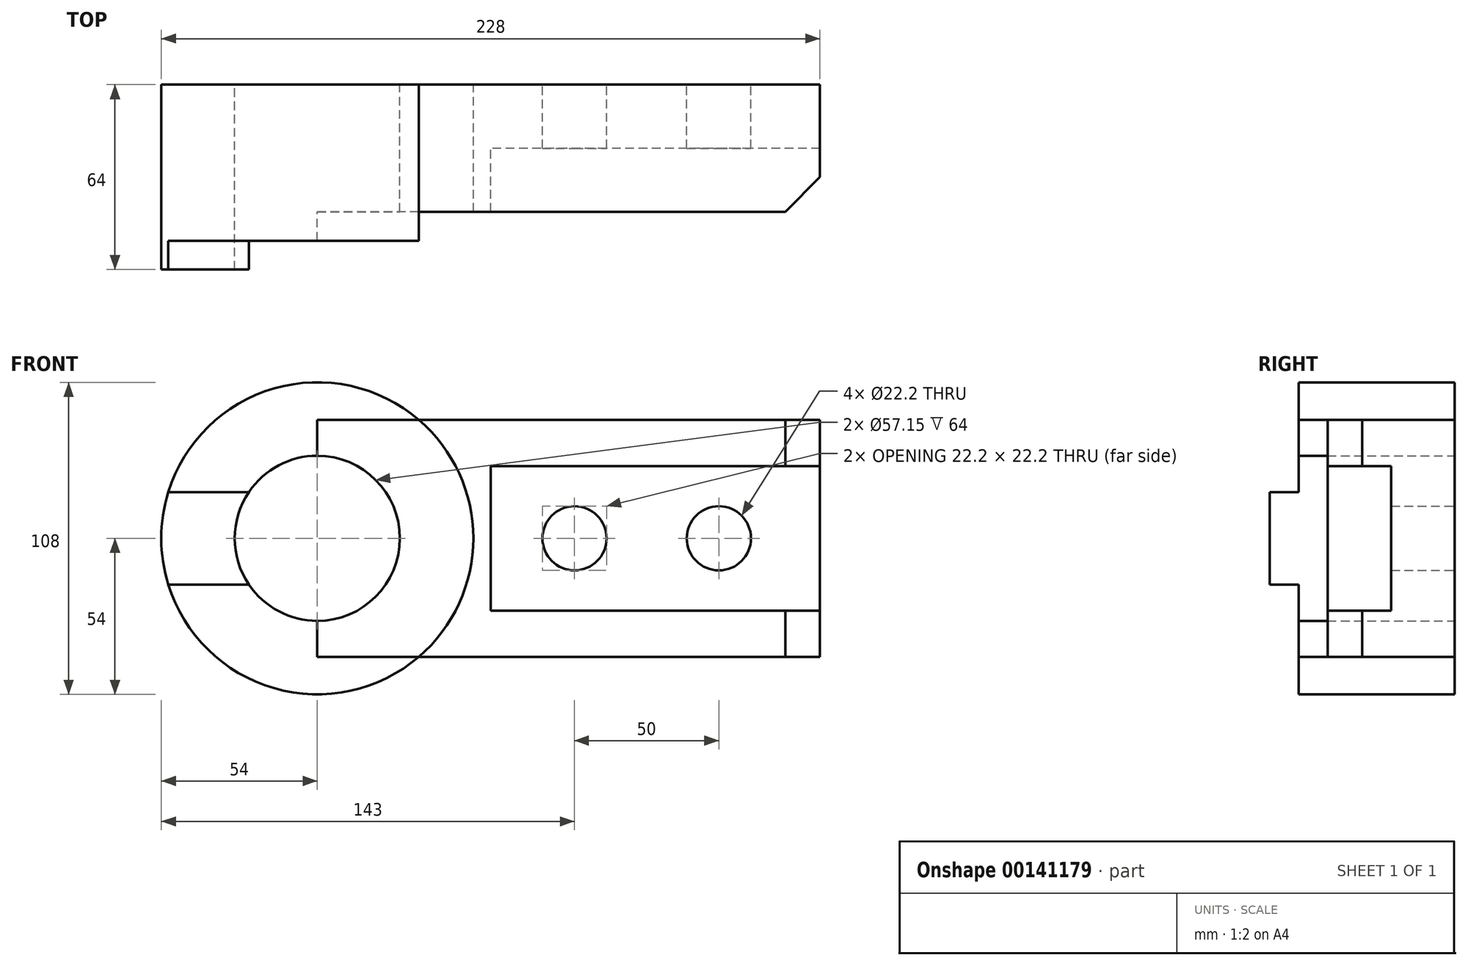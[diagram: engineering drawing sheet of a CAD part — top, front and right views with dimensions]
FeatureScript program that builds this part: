
annotation { "Feature Type Name" : "Feature", "Feature Type Description" : "" }
export const myFeature = defineFeature(function(context is Context, id is Id, definition is map)
    precondition{}
    {
        {
            var Q0;
            Q0=qCreatedBy(makeId("Front.planeOp"),FACE);
            var sketch = newSketch(context, id + "F0", { "sketchPlane" : qUnion([Q0])});
            skCircle(sketch, "E0", {"center": v(0, 0) * mm, "radius": 54 * mm});
            skCircle(sketch, "E1", {"center": v(0, 0) * mm, "radius": 28.57 * mm});
            skLineSegment(sketch, "E2", {"start": v(35.14, 41) * mm, "end": v(174, 41) * mm, "construction": true});
            skLineSegment(sketch, "E3", {"start": v(174, 41) * mm, "end": v(174, -41) * mm, "construction": true});
            skLineSegment(sketch, "E4", {"start": v(174, -41) * mm, "end": v(35.14, -41) * mm, "construction": true});
            skCircle(sketch, "E5", {"center": v(89, 0) * mm, "radius": 11.1 * mm, "construction": true});
            skCircle(sketch, "E6", {"center": v(139, 0) * mm, "radius": 11.1 * mm, "construction": true});
            skLineSegment(sketch, "E7", {"start": v(60, 41) * mm, "end": v(60, -41) * mm, "construction": true});
            skPoint(sketch, "E8", {"position": v(0, 54) * mm});
            skPoint(sketch, "E9", {"position": v(0, -54) * mm});
            skSolve(sketch);
        }
        {
            var Q0;
            Q0 = qSketchRegion(id + "F0", true);
            extrude(context, id + "F1", {"entities" : qUnion([Q0]), "depth" : 64 * mm});
        }
        {
            var Q0;
            Q0=qCreatedBy(makeId("Front.planeOp"),FACE);
            var sketch = newSketch(context, id + "F2", { "sketchPlane" : qUnion([Q0])});
            skLineSegment(sketch, "E10", {"start": v(35.14, 41) * mm, "end": v(174, 41) * mm});
            skLineSegment(sketch, "E11", {"start": v(174, 41) * mm, "end": v(174, -41) * mm});
            skLineSegment(sketch, "E12", {"start": v(174, -41) * mm, "end": v(35.14, -41) * mm});
            skCircle(sketch, "E13", {"center": v(89, 0) * mm, "radius": 11.1 * mm});
            skCircle(sketch, "E14", {"center": v(139, 0) * mm, "radius": 11.1 * mm});
            skArc(sketch, "E15", {"start": v(35.14, 41) * mm, "mid": v(54, 0) * mm, "end": v(35.14, -41) * mm});
            skSolve(sketch);
        }
        {
            var Q0;
            Q0 = qSketchRegion(id + "F2", true);
            extrude(context, id + "F3", {"entities" : qUnion([Q0]), "depth" : 64 * mm});
        }
        {
            var Q0;
            Q0=qCreatedBy(makeId("Right.planeOp"),FACE);
            var sketch = newSketch(context, id + "F4", { "sketchPlane" : qUnion([Q0])});
            skLineSegment(sketch, "E16", {"start": v(-44, -41) * mm, "end": v(-44, 41) * mm});
            skLineSegment(sketch, "E17", {"start": v(-44, -41) * mm, "end": v(-64, -41) * mm});
            skLineSegment(sketch, "E18", {"start": v(-64, -41) * mm, "end": v(-64, 41) * mm});
            skLineSegment(sketch, "E19", {"start": v(-64, 41) * mm, "end": v(-44, 41) * mm});
            skSolve(sketch);
        }
        {
            var Q0;
            Q0 = qSketchRegion(id + "F4", true);
            extrude(context, id + "F5", {"entities" : qUnion([Q0]), "operationType" : NewBodyOperationType.REMOVE, "endBound" : BoundingType.THROUGH_ALL, "depth" : 174 * mm});
        }
        {
            var Q0;
            Q0=qCreatedBy(makeId("Right.planeOp"),FACE);
            var sketch = newSketch(context, id + "F6", { "sketchPlane" : qUnion([Q0])});
            skLineSegment(sketch, "E20", {"start": v(-64, 0) * mm, "end": v(-64, 16) * mm});
            skLineSegment(sketch, "E21", {"start": v(-64, 0) * mm, "end": v(-64, -16) * mm});
            skLineSegment(sketch, "E22", {"start": v(-64, 16) * mm, "end": v(-54, 16) * mm});
            skLineSegment(sketch, "E23", {"start": v(-54, -16) * mm, "end": v(-64, -16) * mm});
            skLineSegment(sketch, "E24", {"start": v(-54, 16) * mm, "end": v(-54, 54.6) * mm});
            skLineSegment(sketch, "E25", {"start": v(-54, 54.6) * mm, "end": v(-64.02, 54.6) * mm});
            skLineSegment(sketch, "E26", {"start": v(-64.02, 54.6) * mm, "end": v(-64, 16) * mm});
            skLineSegment(sketch, "E27", {"start": v(-64, -16) * mm, "end": v(-64, -55.4) * mm});
            skLineSegment(sketch, "E28", {"start": v(-64, -55.4) * mm, "end": v(-54, -55.4) * mm});
            skLineSegment(sketch, "E29", {"start": v(-54, -55.4) * mm, "end": v(-54, -16) * mm});
            skSolve(sketch);
        }
        {
            var Q0;
            Q0 = qSketchRegion(id + "F6", true);
            extrude(context, id + "F7", {"entities" : qUnion([Q0]), "operationType" : NewBodyOperationType.REMOVE, "endBound" : BoundingType.THROUGH_ALL, "oppositeDirection" : true, "depth" : 25 * mm, "hasSecondDirection" : true, "secondDirectionBound" : SecondDirectionBoundingType.THROUGH_ALL, "secondDirectionOppositeDirection" : false, "secondDirectionDepth" : 25 * mm});
        }
        {
            var Q0;
            Q0=qCreatedBy(makeId("Right.planeOp"),FACE);
            var sketch = newSketch(context, id + "F8", { "sketchPlane" : qUnion([Q0])});
            skLineSegment(sketch, "E30", {"start": v(-44, 25) * mm, "end": v(-44, -25) * mm});
            skLineSegment(sketch, "E31", {"start": v(-44, 25) * mm, "end": v(-22, 25) * mm});
            skLineSegment(sketch, "E32", {"start": v(-22, 25) * mm, "end": v(-22, -25) * mm});
            skLineSegment(sketch, "E33", {"start": v(-22, -25) * mm, "end": v(-44, -25) * mm});
            skSolve(sketch);
        }
        {
            var Q0;
            Q0 = qSketchRegion(id + "F8", true);
            extrude(context, id + "F9", {"entities" : qUnion([Q0]), "operationType" : NewBodyOperationType.REMOVE, "depth" : 174 * mm, "hasSecondDirection" : true, "secondDirectionOppositeDirection" : false, "secondDirectionDepth" : 60 * mm});
        }
        {
            var Q0;
            Q0=qCreatedBy(makeId("Top.planeOp"),FACE);
            var sketch = newSketch(context, id + "F10", { "sketchPlane" : qUnion([Q0])});
            skLineSegment(sketch, "E34", {"start": v(174, -44) * mm, "end": v(162, -44) * mm});
            skLineSegment(sketch, "E35", {"start": v(174, -32) * mm, "end": v(162, -44) * mm});
            skLineSegment(sketch, "E36", {"start": v(174, -32) * mm, "end": v(174, -44) * mm});
            skSolve(sketch);
        }
        {
            var Q0;
            Q0 = qSketchRegion(id + "F10", true);
            extrude(context, id + "F11", {"entities" : qUnion([Q0]), "operationType" : NewBodyOperationType.REMOVE, "endBound" : BoundingType.THROUGH_ALL, "depth" : 25 * mm, "hasSecondDirection" : true, "secondDirectionBound" : SecondDirectionBoundingType.THROUGH_ALL, "secondDirectionOppositeDirection" : true, "secondDirectionDepth" : 25 * mm});
        }
    });
